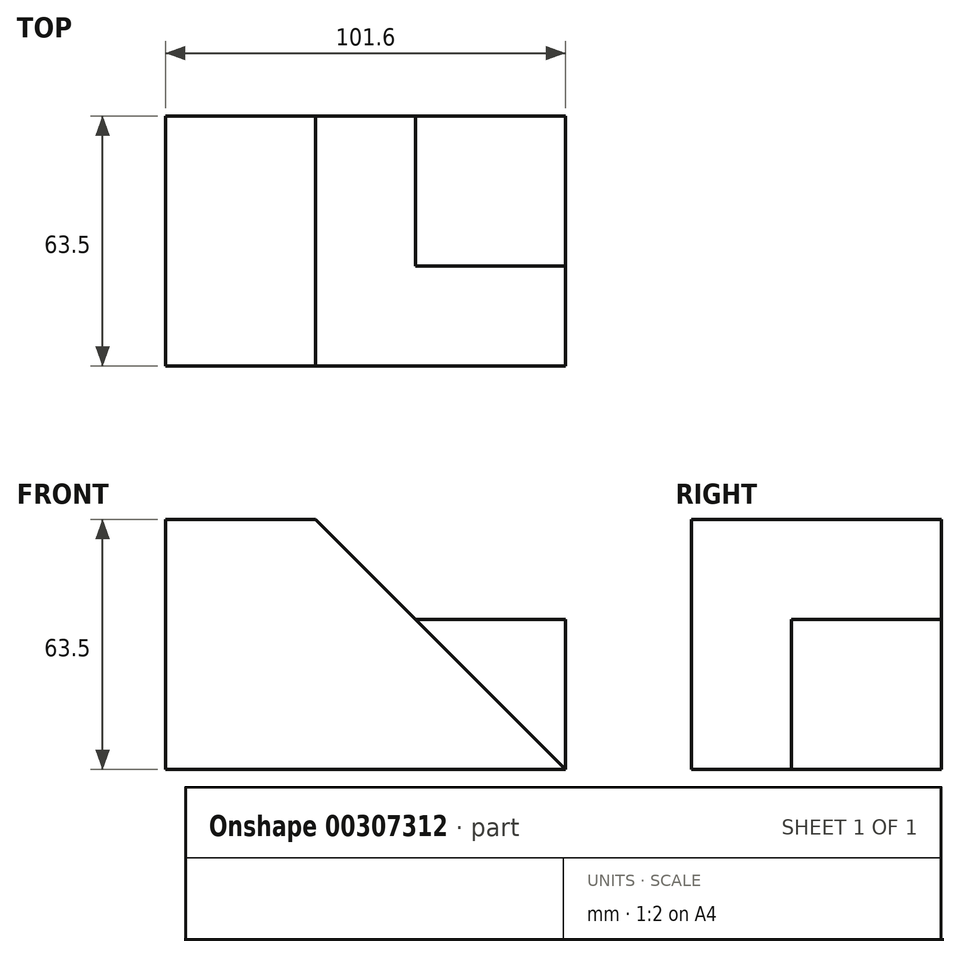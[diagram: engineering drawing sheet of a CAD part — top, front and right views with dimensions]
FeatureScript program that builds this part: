
annotation { "Feature Type Name" : "Feature", "Feature Type Description" : "" }
export const myFeature = defineFeature(function(context is Context, id is Id, definition is map)
    precondition{}
    {
        {
            var Q0;
            Q0=qCreatedBy(makeId("Front.planeOp"),FACE);
            var sketch = newSketch(context, id + "F0", { "sketchPlane" : qUnion([Q0])});
            skLineSegment(sketch, "E0", {"start": v(-48.54, 50.75) * mm, "end": v(-86.64, 50.75) * mm});
            skLineSegment(sketch, "E1", {"start": v(-86.64, 50.75) * mm, "end": v(-86.64, -12.75) * mm});
            skLineSegment(sketch, "E2", {"start": v(-86.64, -12.75) * mm, "end": v(14.96, -12.75) * mm});
            skLineSegment(sketch, "E3", {"start": v(14.96, -12.75) * mm, "end": v(-48.54, 50.75) * mm});
            skSolve(sketch);
        }
        {
            var Q0;
            Q0=makeQuery(id+"F0.imprint","IMPRINT",FACE,{"disambiguationData":[TD([[makeQuery(id+"F0.imprint","IMPRINT",EDGE,{"derivedFrom":sQuery(id+"F0.wireOp",EDGE,"E0")}),1.0]])]});
            extrude(context, id + "F1", {"entities" : qUnion([Q0]), "depth" : 63.5 * mm});
        }
        {
            var Q0;
            Q0=makeQuery(id+"F1.opExtrude","CAP_FACE",FACE,{"disambiguationData":[OSD([sQuery(id+"F0.wireOp",EDGE,"E0"),sQuery(id+"F0.wireOp",EDGE,"E1"),sQuery(id+"F0.wireOp",EDGE,"E2"),sQuery(id+"F0.wireOp",EDGE,"E3")])],"isStart":true});
            var sketch = newSketch(context, id + "F2", { "sketchPlane" : qUnion([Q0])});
            skLineSegment(sketch, "E4", {"start": v(23.14, 25.35) * mm, "end": v(-14.96, 25.35) * mm});
            skLineSegment(sketch, "E5", {"start": v(-14.96, 25.35) * mm, "end": v(-14.96, -12.75) * mm});
            skLineSegment(sketch, "E6", {"start": v(-14.96, -12.75) * mm, "end": v(23.14, 25.35) * mm});
            skSolve(sketch);
        }
        {
            var Q0;
            Q0=makeQuery(id+"F2.imprint","IMPRINT",FACE,{"disambiguationData":[TD([[makeQuery(id+"F2.imprint","IMPRINT",EDGE,{"derivedFrom":sQuery(id+"F2.wireOp",EDGE,"E4")}),1.0]])]});
            extrude(context, id + "F3", {"entities" : qUnion([Q0]), "operationType" : NewBodyOperationType.ADD, "oppositeDirection" : true, "depth" : 38.1 * mm});
        }
    });
